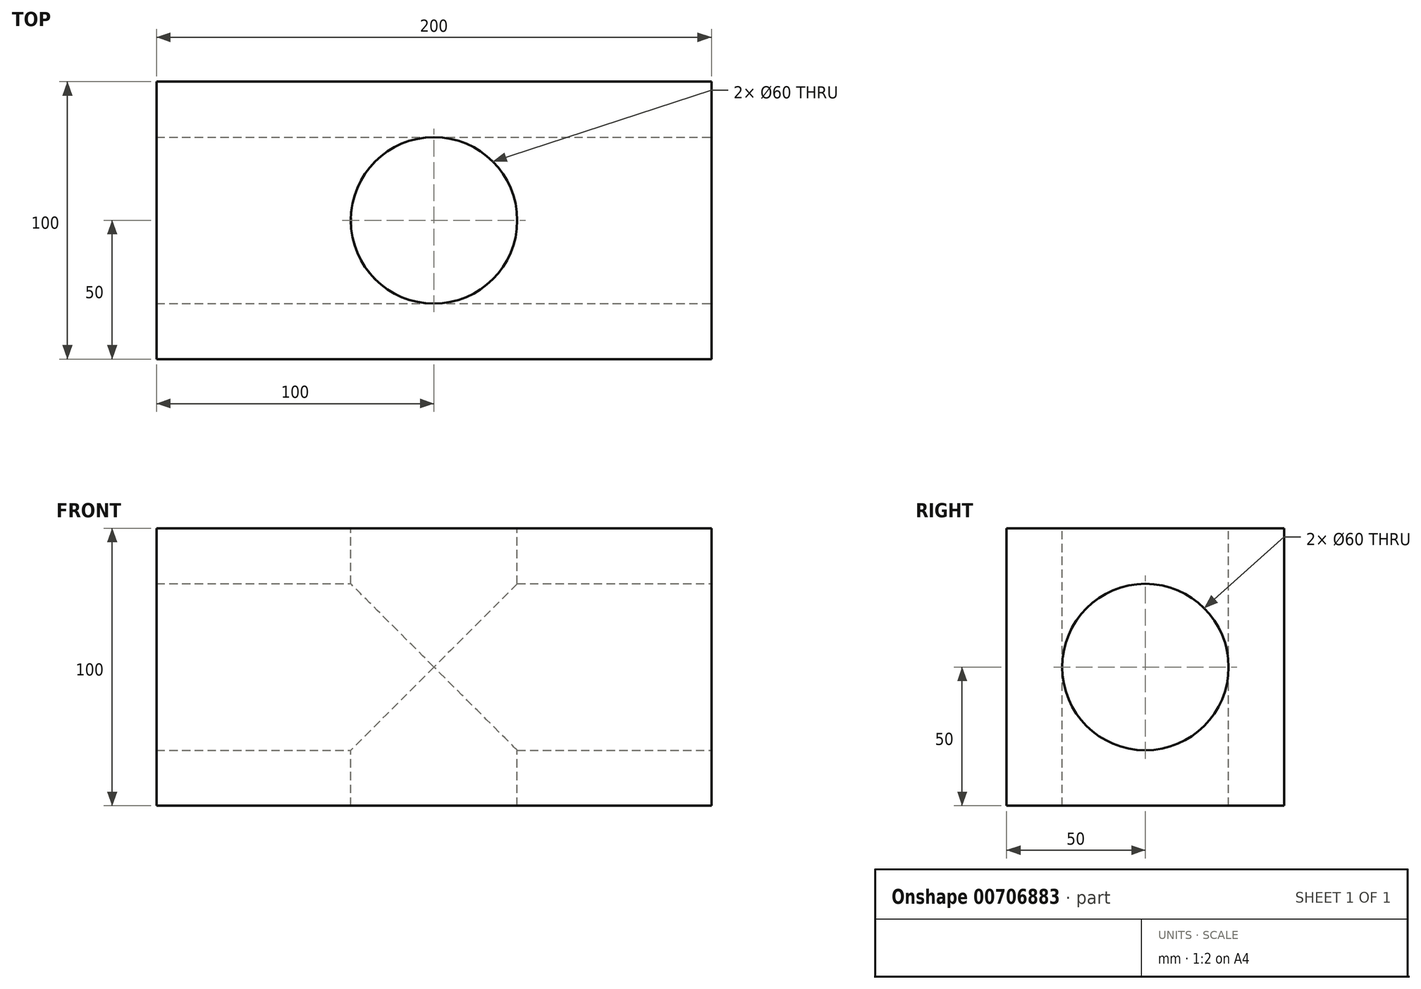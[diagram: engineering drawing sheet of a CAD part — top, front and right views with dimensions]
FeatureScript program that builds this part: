
annotation { "Feature Type Name" : "Feature", "Feature Type Description" : "" }
export const myFeature = defineFeature(function(context is Context, id is Id, definition is map)
    precondition{}
    {
        {
            var Q0;
            Q0=qCreatedBy(makeId("Top.planeOp"),FACE);
            var sketch = newSketch(context, id + "F0", { "sketchPlane" : qUnion([Q0])});
            skLineSegment(sketch, "E0.bottom", {"start": v(-100, 50) * mm, "end": v(100, 50) * mm});
            skLineSegment(sketch, "E0.top", {"start": v(-100, -50) * mm, "end": v(100, -50) * mm});
            skLineSegment(sketch, "E0.left", {"start": v(-100, 50) * mm, "end": v(-100, -50) * mm});
            skLineSegment(sketch, "E0.right", {"start": v(100, 50) * mm, "end": v(100, -50) * mm});
            skSolve(sketch);
        }
        {
            var Q0;
            Q0=makeQuery(id+"F0.imprint","IMPRINT",FACE,{"disambiguationData":[TD([[makeQuery(id+"F0.imprint","IMPRINT",EDGE,{"derivedFrom":sQuery(id+"F0.wireOp",EDGE,"E0.bottom")}),-1.0]])]});
            extrude(context, id + "F1", {"entities" : qUnion([Q0]), "depth" : 100 * mm, "offsetDistance" : 25 * mm});
        }
        {
            var Q0;
            Q0=makeQuery(id+"F1.opExtrude","CAP_FACE",FACE,{"disambiguationData":[OSD([sQuery(id+"F0.wireOp",EDGE,"E0.bottom"),sQuery(id+"F0.wireOp",EDGE,"E0.top"),sQuery(id+"F0.wireOp",EDGE,"E0.left"),sQuery(id+"F0.wireOp",EDGE,"E0.right")])],"isStart":false});
            var sketch = newSketch(context, id + "F2", { "sketchPlane" : qUnion([Q0])});
            skCircle(sketch, "E1", {"center": v(0, 0) * mm, "radius": 30 * mm});
            skSolve(sketch);
        }
        {
            var Q0;
            Q0=makeQuery(id+"F2.imprint","IMPRINT",FACE,{"disambiguationData":[TD([[makeQuery(id+"F2.imprint","IMPRINT",EDGE,{"derivedFrom":sQuery(id+"F2.wireOp",EDGE,"E1")}),1.0]])]});
            extrude(context, id + "F3", {"entities" : qUnion([Q0]), "operationType" : NewBodyOperationType.REMOVE, "endBound" : BoundingType.UP_TO_NEXT, "oppositeDirection" : true, "depth" : 25 * mm, "offsetDistance" : 25 * mm});
        }
        {
            var Q0;
            Q0=makeQuery(id+"F1.opExtrude","SWEPT_FACE",FACE,{"disambiguationData":[OSD([sQuery(id+"F0.wireOp",EDGE,"E0.right")])]});
            var sketch = newSketch(context, id + "F4", { "sketchPlane" : qUnion([Q0])});
            skCircle(sketch, "E2", {"center": v(0, 50) * mm, "radius": 30 * mm});
            skSolve(sketch);
        }
        {
            var Q0;
            Q0 = qSketchRegion(id + "F4", true);
            extrude(context, id + "F5", {"entities" : qUnion([Q0]), "operationType" : NewBodyOperationType.REMOVE, "endBound" : BoundingType.THROUGH_ALL, "oppositeDirection" : true, "depth" : 25 * mm, "offsetDistance" : 25 * mm});
        }
    });
